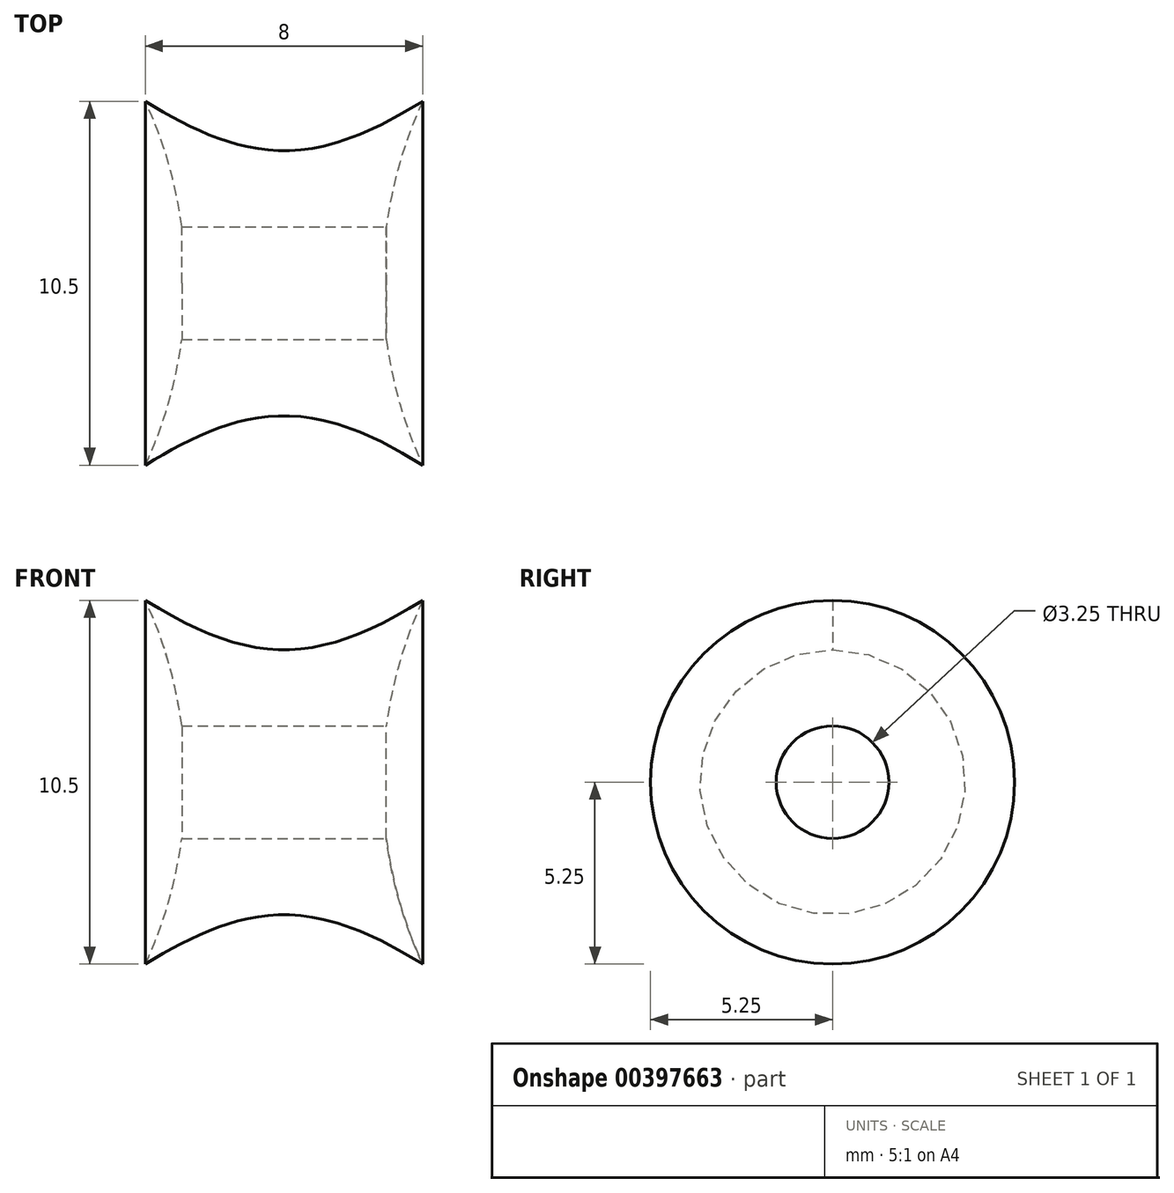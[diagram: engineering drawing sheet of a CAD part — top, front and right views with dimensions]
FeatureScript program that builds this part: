
annotation { "Feature Type Name" : "Feature", "Feature Type Description" : "" }
export const myFeature = defineFeature(function(context is Context, id is Id, definition is map)
    precondition{}
    {
        {
            var Q0;
            Q0=qCreatedBy(makeId("Top.planeOp"),FACE);
            var sketch = newSketch(context, id + "F0", { "sketchPlane" : qUnion([Q0])});
            skArc(sketch, "E0", {"start": v(-28.87, 0) * mm, "mid": v(-16.37, 12.5) * mm, "end": v(-3.87, 0) * mm});
            skLineSegment(sketch, "E1", {"start": v(-28.87, 0) * mm, "end": v(26.82, 0) * mm});
            skArc(sketch, "E2", {"start": v(26.82, 0) * mm, "mid": v(14.32, 12.5) * mm, "end": v(1.82, 0) * mm});
            skFitSpline(sketch, "E3", {"points": [v(-5.03, 5.25) * mm, v(2.97, 5.25) * mm], "startDerivative": vector(9.15, -5.7) * mm, "endDerivative": vector(9.15, 5.7) * mm});
            skSolve(sketch);
        }
        {
            var Q0;
            {var subQ0=sQuery(id+"F0.wireOp",EDGE,"E2");var subQ1=sQuery(id+"F0.wireOp",EDGE,"E1");var subQ2=makeQuery(id+"F0.imprint","INTERSECT",VERTEX,{"disambiguationData":[OD(0.0)],"derivedFrom":[subQ1,subQ0]});Q0=makeQuery(id+"F0.imprint","IMPRINT",FACE,{"disambiguationData":[TD([[makeQuery(id+"F0.imprint","IMPRINT",EDGE,{"disambiguationData":[TD([[subQ2,1.0]])],"derivedFrom":subQ1}),1.0]])]});}
            var Q1;
            {var subQ0=sQuery(id+"F0.wireOp",EDGE,"E1");var subQ1=sQuery(id+"F0.wireOp",EDGE,"E0");var subQ2=makeQuery(id+"F0.imprint","INTERSECT",VERTEX,{"disambiguationData":[OD(0.0)],"derivedFrom":[subQ1,subQ0]});Q1=makeQuery(id+"F0.imprint","IMPRINT",FACE,{"disambiguationData":[TD([[makeQuery(id+"F0.imprint","IMPRINT",EDGE,{"disambiguationData":[TD([[subQ2,-1.0]])],"derivedFrom":subQ1}),-1.0]])]});}
            var Q2;
            {var subQ3=sQuery(id+"F0.wireOp",EDGE,"E3");Q2=makeQuery(id+"F0.imprint","IMPRINT",FACE,{"disambiguationData":[TD([[makeQuery(id+"F0.imprint","IMPRINT",EDGE,{"derivedFrom":subQ3}),-1.0]])]});}
            var Q3;
            Q3=sQuery(id+"F0.wireOp",EDGE,"E1");
            revolve(context, id + "F1", {"entities" : qUnion([Q0, Q1, Q2]), "axis" : qUnion([Q3]), "revolveType" : RevolveType.FULL});
        }
        {
            var Q0;
            Q0=qCreatedBy(makeId("Right.planeOp"),FACE);
            var Q1;
            Q1=sQuery(id+"F0.wireOp",VERTEX,"E2.start");
            cPlane(context, id + "F2", {"entities" : qUnion([Q0, Q1]), "cplaneType" : CPlaneType.PLANE_POINT, "offset" : 25 * mm, "width" : 150 * mm, "height" : 150 * mm});
        }
        {
            var Q0;
            Q0=qCreatedBy(id+"F2.planeOp",FACE);
            var sketch = newSketch(context, id + "F3", { "sketchPlane" : qUnion([Q0])});
            skCircle(sketch, "E4", {"center": v(0, 0) * mm, "radius": 1.62 * mm});
            skSolve(sketch);
        }
        {
            var Q0;
            Q0=qCreatedBy(makeId("Top.planeOp"),FACE);
            cPlane(context, id + "F4", {"entities" : qUnion([Q0]), "cplaneType" : CPlaneType.OFFSET, "offset" : 9.5 * mm, "width" : 150 * mm, "height" : 150 * mm});
        }
        {
            var Q0;
            Q0=qCreatedBy(id+"F4.planeOp",FACE);
            var sketch = newSketch(context, id + "F5", { "sketchPlane" : qUnion([Q0])});
            skCircle(sketch, "E5", {"center": v(15.8, 0) * mm, "radius": 25 * mm});
            skCircle(sketch, "E6", {"center": v(-17.28, 1.86) * mm, "radius": 22.82 * mm});
            skSolve(sketch);
        }
        {
            var Q0;
            Q0 = qSketchRegion(id + "F5", true);
            extrude(context, id + "F6", {"entities" : qUnion([Q0]), "operationType" : NewBodyOperationType.REMOVE, "depth" : 25 * mm});
        }
        {
            var Q0;
            Q0 = qSketchRegion(id + "F3", true);
            extrude(context, id + "F7", {"entities" : qUnion([Q0]), "operationType" : NewBodyOperationType.REMOVE, "endBound" : BoundingType.THROUGH_ALL, "oppositeDirection" : true, "depth" : 25 * mm});
        }
    });
